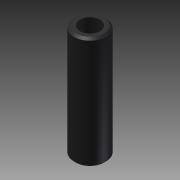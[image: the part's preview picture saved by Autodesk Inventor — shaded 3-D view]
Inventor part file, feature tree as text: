
AUTODESK INVENTOR PART (.ipt)
format: ipt  version: 2015 (Build 190159000, 159)  size: 92,672 bytes
history: native  units: mm
features: extrude x1, chamfer x1
ambient origin geometry x8: Origin, YZ Plane, XZ Plane, XY Plane, X Axis, Y Axis, Z Axis, Center Point
bodies: Solid1 (feature_tree)
feature tree (2):
  extrude  "Extrusión1"  Depth=5.0mm
  chamfer  "Chaflán1"  Distance=8.0mm
